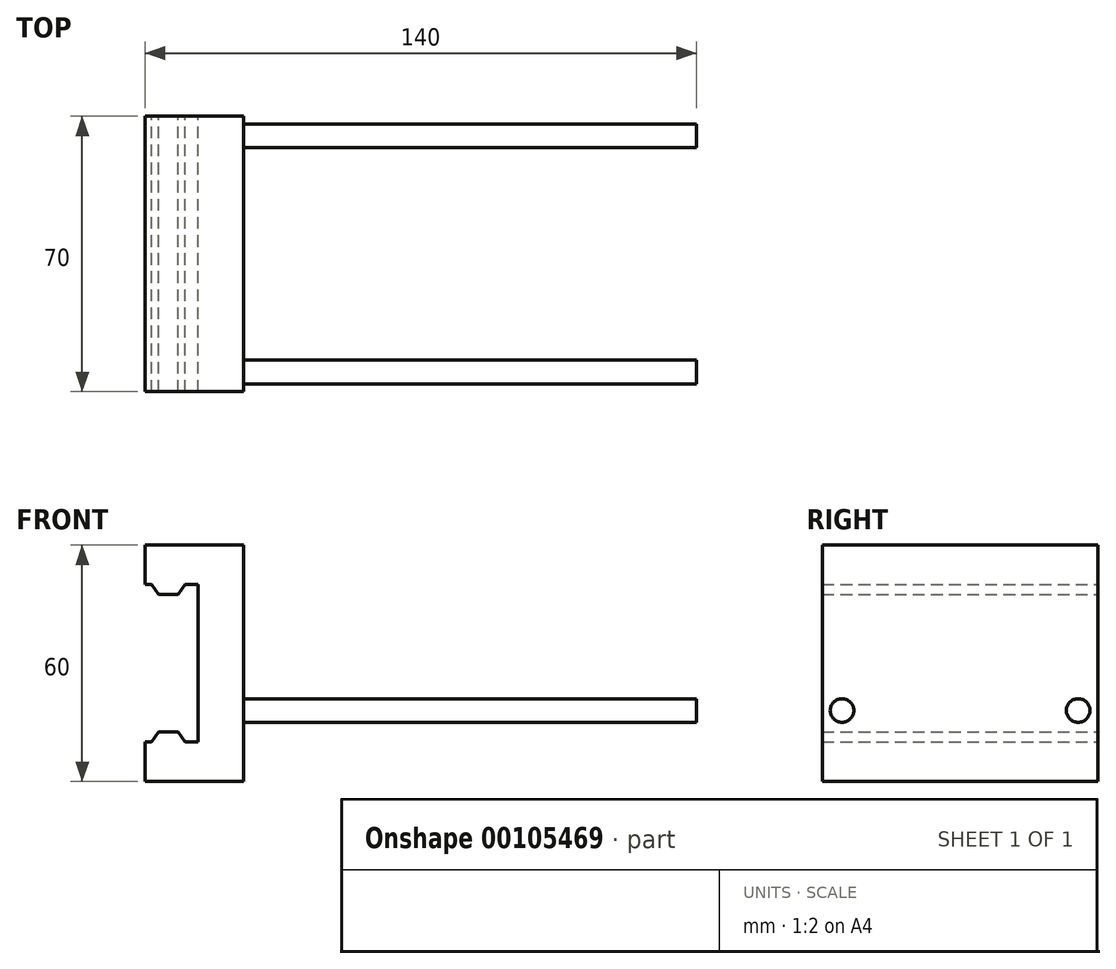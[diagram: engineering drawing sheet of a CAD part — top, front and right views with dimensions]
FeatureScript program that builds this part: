
annotation { "Feature Type Name" : "Feature", "Feature Type Description" : "" }
export const myFeature = defineFeature(function(context is Context, id is Id, definition is map)
    precondition{}
    {
        {
            var Q0;
            Q0=qCreatedBy(makeId("Front.planeOp"),FACE);
            var sketch = newSketch(context, id + "F0", { "sketchPlane" : qUnion([Q0])});
            skLineSegment(sketch, "E0.bottom", {"start": v(-7.96, 16.54) * mm, "end": v(-6.34, 16.54) * mm});
            skLineSegment(sketch, "E0.right", {"start": v(5.41, 16.54) * mm, "end": v(5.41, -23.46) * mm});
            skLineSegment(sketch, "E1.bottom", {"start": v(0.41, 14.04) * mm, "end": v(-4.59, 14.04) * mm});
            skLineSegment(sketch, "E1.top", {"start": v(0.41, -20.96) * mm, "end": v(-4.59, -20.96) * mm});
            skPoint(sketch, "E1.middle", {"position": v(-2.09, -3.46) * mm});
            skPoint(sketch, "E1.middle.positionSnap0", {"position": v(-9.59, -3.46) * mm});
            skPoint(sketch, "E1.middle.positionSnap1", {"position": v(-2.09, 16.54) * mm});
            skPoint(sketch, "E1.centerSnap0", {"position": v(-9.59, -3.46) * mm});
            skPoint(sketch, "E1.centerSnap1", {"position": v(-2.09, 16.54) * mm});
            skLineSegment(sketch, "E2", {"start": v(0.41, 14.04) * mm, "end": v(2.16, 16.54) * mm});
            skLineSegment(sketch, "E3", {"start": v(-4.59, 14.04) * mm, "end": v(-6.34, 16.54) * mm});
            skLineSegment(sketch, "E4.trimOffspring", {"start": v(2.16, 16.54) * mm, "end": v(5.41, 16.54) * mm});
            skLineSegment(sketch, "E5", {"start": v(-7.96, 16.54) * mm, "end": v(-7.96, 26.54) * mm});
            skPoint(sketch, "E6.orphan", {"position": v(-9.59, 16.54) * mm});
            skPoint(sketch, "E0.top.start.orphan", {"position": v(-9.59, -23.46) * mm});
            skLineSegment(sketch, "E7.MirrorCS", {"start": v(0.41, -20.96) * mm, "end": v(2.16, -23.46) * mm});
            skLineSegment(sketch, "E8.MirrorCS", {"start": v(2.16, -23.46) * mm, "end": v(5.41, -23.46) * mm});
            skLineSegment(sketch, "E9.MirrorCS", {"start": v(-4.59, -20.96) * mm, "end": v(-6.34, -23.46) * mm});
            skLineSegment(sketch, "E10.MirrorCS", {"start": v(-7.96, -23.46) * mm, "end": v(-6.34, -23.46) * mm});
            skLineSegment(sketch, "E11.MirrorCS", {"start": v(-7.96, -23.46) * mm, "end": v(-7.96, -33.46) * mm});
            skLineSegment(sketch, "E12", {"start": v(-7.96, 26.54) * mm, "end": v(17.04, 26.54) * mm});
            skLineSegment(sketch, "E13", {"start": v(17.04, 26.54) * mm, "end": v(17.04, -33.46) * mm});
            skLineSegment(sketch, "E14", {"start": v(17.04, -33.46) * mm, "end": v(-7.96, -33.46) * mm});
            skSolve(sketch);
        }
        {
            var Q0;
            Q0 = qSketchRegion(id + "F0", true);
            extrude(context, id + "F1", {"entities" : qUnion([Q0]), "depth" : 70 * mm});
        }
        {
            var Q0;
            Q0=makeQuery(id+"F1.opExtrude","SWEPT_FACE",FACE,{"disambiguationData":[OSD([sQuery(id+"F0.wireOp",EDGE,"E13")])]});
            var sketch = newSketch(context, id + "F2", { "sketchPlane" : qUnion([Q0])});
            skCircle(sketch, "E15", {"center": v(-65, -15.46) * mm, "radius": 3 * mm});
            skCircle(sketch, "E16", {"center": v(-5, -15.46) * mm, "radius": 3 * mm});
            skSolve(sketch);
        }
        {
            var Q0;
            Q0 = qSketchRegion(id + "F2", true);
            extrude(context, id + "F3", {"entities" : qUnion([Q0]), "operationType" : NewBodyOperationType.ADD, "depth" : 115 * mm});
        }
    });
